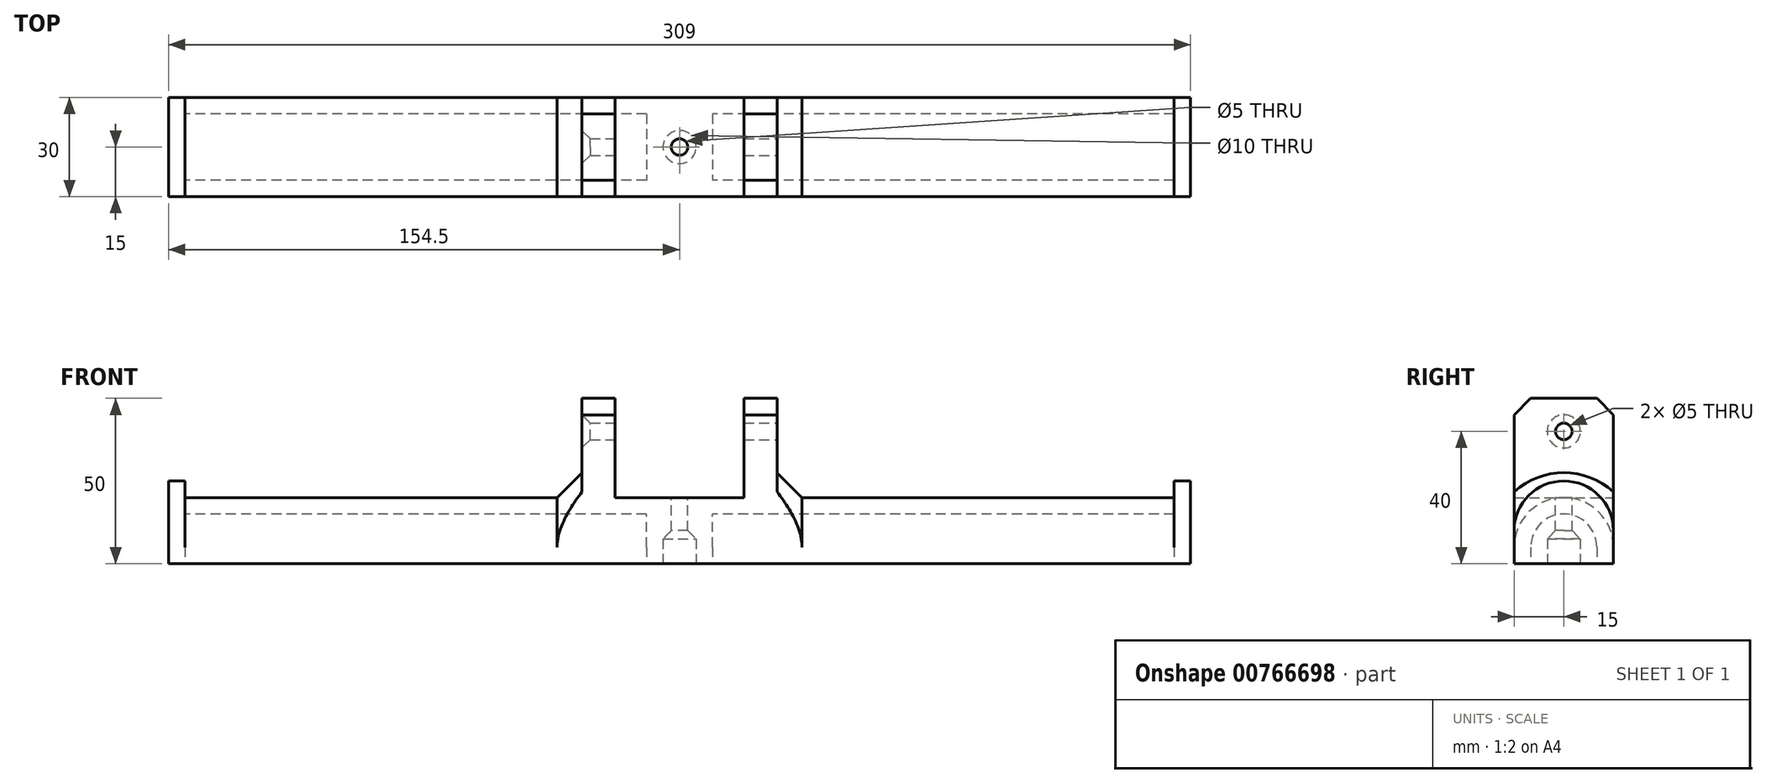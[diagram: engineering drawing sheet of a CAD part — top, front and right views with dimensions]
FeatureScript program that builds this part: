
annotation { "Feature Type Name" : "Feature", "Feature Type Description" : "" }
export const myFeature = defineFeature(function(context is Context, id is Id, definition is map)
    precondition{}
    {
        {
            var Q0;
            Q0=qCreatedBy(makeId("Front.planeOp"),FACE);
            var sketch = newSketch(context, id + "F0", { "sketchPlane" : qUnion([Q0])});
            skLineSegment(sketch, "E0", {"start": v(0, 0) * mm, "end": v(0, 100) * mm, "construction": true});
            skLineSegment(sketch, "E1", {"start": v(0, 0) * mm, "end": v(149.5, 0) * mm});
            skLineSegment(sketch, "E2", {"start": v(149.5, 0) * mm, "end": v(149.5, 20) * mm});
            skLineSegment(sketch, "E3", {"start": v(149.5, 20) * mm, "end": v(29.5, 20) * mm});
            skLineSegment(sketch, "E4", {"start": v(29.5, 20) * mm, "end": v(29.5, 50) * mm});
            skLineSegment(sketch, "E5", {"start": v(29.5, 50) * mm, "end": v(19.5, 50) * mm});
            skLineSegment(sketch, "E6", {"start": v(19.5, 50) * mm, "end": v(19.5, 20) * mm});
            skLineSegment(sketch, "E7", {"start": v(19.5, 20) * mm, "end": v(0, 20) * mm});
            skLineSegment(sketch, "E8.MirrorCS", {"start": v(0, 0) * mm, "end": v(-149.5, 0) * mm});
            skLineSegment(sketch, "E9.MirrorCS", {"start": v(-19.5, 20) * mm, "end": v(0, 20) * mm});
            skLineSegment(sketch, "E10.MirrorCS", {"start": v(-19.5, 50) * mm, "end": v(-19.5, 20) * mm});
            skLineSegment(sketch, "E11.MirrorCS", {"start": v(-149.5, 0) * mm, "end": v(-149.5, 20) * mm});
            skLineSegment(sketch, "E12.MirrorCS", {"start": v(-29.5, 20) * mm, "end": v(-29.5, 50) * mm});
            skLineSegment(sketch, "E13.MirrorCS", {"start": v(-29.5, 50) * mm, "end": v(-19.5, 50) * mm});
            skLineSegment(sketch, "E14.MirrorCS", {"start": v(-149.5, 20) * mm, "end": v(-29.5, 20) * mm});
            skSolve(sketch);
        }
        {
            var Q0;
            Q0 = qSketchRegion(id + "F0", true);
            extrude(context, id + "F1", {"entities" : qUnion([Q0]), "depth" : 30 * mm, "offsetDistance" : 25 * mm});
        }
        {
            var Q0;
            Q0=makeQuery(id+"F1.opExtrude","CAP_EDGE",EDGE,{"disambiguationData":[OSD([sQuery(id+"F0.wireOp",EDGE,"E14.MirrorCS")])],"isStart":true});
            var Q1;
            Q1=makeQuery(id+"F1.opExtrude","CAP_EDGE",EDGE,{"disambiguationData":[OSD([sQuery(id+"F0.wireOp",EDGE,"E14.MirrorCS")])],"isStart":false});
            var Q2;
            Q2=makeQuery(id+"F1.opExtrude","CAP_EDGE",EDGE,{"disambiguationData":[OSD([sQuery(id+"F0.wireOp",EDGE,"E3")])],"isStart":true});
            var Q3;
            Q3=makeQuery(id+"F1.opExtrude","CAP_EDGE",EDGE,{"disambiguationData":[OSD([sQuery(id+"F0.wireOp",EDGE,"E3")])],"isStart":false});
            fillet(context, id + "F2", {"entities" : qUnion([Q0, Q1, Q2, Q3]), "radius" : 15 * mm, "tangentPropagation" : true, "allowEdgeOverflow" : false});
        }
        {
            var Q0;
            Q0=makeQuery(id+"F1.opExtrude","SWEPT_FACE",FACE,{"disambiguationData":[OSD([sQuery(id+"F0.wireOp",EDGE,"E11.MirrorCS")])]});
            var sketch = newSketch(context, id + "F3", { "sketchPlane" : qUnion([Q0])});
            skArc(sketch, "E15.0", {"start": v(25, 5) * mm, "mid": v(15, 15) * mm, "end": v(5, 5) * mm});
            skLineSegment(sketch, "E16.bottom", {"start": v(5, 5) * mm, "end": v(25, 5) * mm, "construction": true});
            skLineSegment(sketch, "E16.top", {"start": v(5, 0) * mm, "end": v(25, 0) * mm});
            skLineSegment(sketch, "E16.left", {"start": v(5, 5) * mm, "end": v(5, 0) * mm});
            skLineSegment(sketch, "E16.right", {"start": v(25, 5) * mm, "end": v(25, 0) * mm});
            skSolve(sketch);
        }
        {
            var Q0;
            Q0 = qSketchRegion(id + "F3", true);
            extrude(context, id + "F4", {"entities" : qUnion([Q0]), "operationType" : NewBodyOperationType.REMOVE, "endBound" : BoundingType.THROUGH_ALL, "oppositeDirection" : true, "depth" : 25 * mm, "offsetDistance" : 25 * mm});
        }
        {
            var Q0;
            Q0=makeQuery(id+"F2.opFillet","BLEND_EDGE",EDGE,{"blendedFrom":[makeQuery(id+"F1.opExtrude","CAP_EDGE",EDGE,{"disambiguationData":[OSD([sQuery(id+"F0.wireOp",EDGE,"E14.MirrorCS")])],"isStart":true}),makeQuery(id+"F1.opExtrude","SWEPT_FACE",FACE,{"disambiguationData":[OSD([sQuery(id+"F0.wireOp",EDGE,"E12.MirrorCS")])]})],"blendedInto":[makeQuery(id+"F1.opExtrude","SWEPT_FACE",FACE,{"disambiguationData":[OSD([sQuery(id+"F0.wireOp",EDGE,"E12.MirrorCS")])]})]});
            var Q1;
            Q1=makeQuery(id+"F2.opFillet","BLEND_EDGE",EDGE,{"blendedFrom":[makeQuery(id+"F1.opExtrude","CAP_EDGE",EDGE,{"disambiguationData":[OSD([sQuery(id+"F0.wireOp",EDGE,"E3")])],"isStart":true}),makeQuery(id+"F1.opExtrude","SWEPT_FACE",FACE,{"disambiguationData":[OSD([sQuery(id+"F0.wireOp",EDGE,"E4")])]})],"blendedInto":[makeQuery(id+"F1.opExtrude","SWEPT_FACE",FACE,{"disambiguationData":[OSD([sQuery(id+"F0.wireOp",EDGE,"E4")])]})]});
            chamfer(context, id + "F5", {"entities" : qUnion([Q0, Q1]), "width" : 7.5 * mm, "tangentPropagation" : true});
        }
        {
            var Q0;
            Q0=makeQuery(id+"F1.opExtrude","CAP_EDGE",EDGE,{"disambiguationData":[OSD([sQuery(id+"F0.wireOp",EDGE,"E13.MirrorCS")])],"isStart":true});
            var Q1;
            Q1=makeQuery(id+"F1.opExtrude","CAP_EDGE",EDGE,{"disambiguationData":[OSD([sQuery(id+"F0.wireOp",EDGE,"E13.MirrorCS")])],"isStart":false});
            var Q2;
            Q2=makeQuery(id+"F1.opExtrude","CAP_EDGE",EDGE,{"disambiguationData":[OSD([sQuery(id+"F0.wireOp",EDGE,"E5")])],"isStart":true});
            var Q3;
            Q3=makeQuery(id+"F1.opExtrude","CAP_EDGE",EDGE,{"disambiguationData":[OSD([sQuery(id+"F0.wireOp",EDGE,"E5")])],"isStart":false});
            chamfer(context, id + "F6", {"entities" : qUnion([Q0, Q1, Q2, Q3]), "width" : 5 * mm, "tangentPropagation" : true});
        }
        {
            var Q0;
            Q0=makeQuery(id+"F1.opExtrude","SWEPT_FACE",FACE,{"disambiguationData":[OSD([sQuery(id+"F0.wireOp",EDGE,"E4")])]});
            var sketch = newSketch(context, id + "F7", { "sketchPlane" : qUnion([Q0])});
            skCircle(sketch, "E17", {"center": v(-15, 40) * mm, "radius": 2.5 * mm});
            skPoint(sketch, "E17.centerSnap0", {"position": v(-15, 50) * mm});
            skSolve(sketch);
        }
        {
            var Q0;
            Q0 = qSketchRegion(id + "F7", true);
            extrude(context, id + "F8", {"entities" : qUnion([Q0]), "operationType" : NewBodyOperationType.REMOVE, "endBound" : BoundingType.THROUGH_ALL, "oppositeDirection" : true, "depth" : 25 * mm, "offsetDistance" : 25 * mm});
        }
        {
            var Q0;
            {var subQ1=sQuery(id+"F0.wireOp",EDGE,"E8.MirrorCS");var subQ3=sQuery(id+"F0.wireOp",EDGE,"E1");Q0=makeQuery(id+"F4.boolean.opBoolean","SPLIT",FACE,{"disambiguationData":[TD([makeQuery(id+"F4.opExtrude","SWEPT_FACE",FACE,{"disambiguationData":[OSD([sQuery(id+"F3.wireOp",EDGE,"E16.right")])]})])],"derivedFrom":makeQuery(id+"F1.opExtrude","SWEPT_FACE",FACE,{"disambiguationData":[OSD([subQ3,subQ1])]})});}
            var sketch = newSketch(context, id + "F9", { "sketchPlane" : qUnion([Q0])});
            skLineSegment(sketch, "E18.0.0", {"start": v(19.5, 0) * mm, "end": v(-19.5, 0) * mm, "construction": true});
            skLineSegment(sketch, "E18.0.1", {"start": v(-19.5, 0) * mm, "end": v(-19.5, 30) * mm, "construction": true});
            skLineSegment(sketch, "E18.0.2", {"start": v(-19.5, 30) * mm, "end": v(19.5, 30) * mm, "construction": true});
            skLineSegment(sketch, "E18.0.3", {"start": v(19.5, 30) * mm, "end": v(19.5, 0) * mm, "construction": true});
            skLineSegment(sketch, "E19.bottom", {"start": v(10, 5) * mm, "end": v(-10, 5) * mm});
            skLineSegment(sketch, "E19.top", {"start": v(10, 25) * mm, "end": v(-10, 25) * mm});
            skLineSegment(sketch, "E19.left", {"start": v(10, 5) * mm, "end": v(10, 25) * mm});
            skLineSegment(sketch, "E19.right", {"start": v(-10, 5) * mm, "end": v(-10, 25) * mm});
            skPoint(sketch, "E19.middle", {"position": v(0, 15) * mm});
            skSolve(sketch);
        }
        {
            var Q0;
            Q0 = qSketchRegion(id + "F9", true);
            var Q1;
            Q1=makeQuery(id+"F4.boolean.opBoolean","COPY",FACE,{"derivedFrom":makeQuery(id+"F4.opExtrude","SWEPT_FACE",FACE,{"disambiguationData":[OSD([sQuery(id+"F3.wireOp",EDGE,"E15.0")])]})});
            extrude(context, id + "F10", {"entities" : qUnion([Q0]), "operationType" : NewBodyOperationType.ADD, "endBound" : BoundingType.UP_TO_SURFACE, "oppositeDirection" : true, "depth" : 25 * mm, "endBoundEntityFace" : qUnion([Q1]), "offsetDistance" : 25 * mm});
        }
        {
            var Q0;
            Q0=makeQuery(id+"F1.opExtrude","SWEPT_FACE",FACE,{"disambiguationData":[OSD([sQuery(id+"F0.wireOp",EDGE,"E7"),sQuery(id+"F0.wireOp",EDGE,"E9.MirrorCS")])]});
            var sketch = newSketch(context, id + "F11", { "sketchPlane" : qUnion([Q0])});
            skCircle(sketch, "E20", {"center": v(0, -15) * mm, "radius": 2.5 * mm});
            skPoint(sketch, "E20.centerSnap0", {"position": v(19.5, -15) * mm});
            skSolve(sketch);
        }
        {
            var Q0;
            Q0 = qSketchRegion(id + "F11", true);
            extrude(context, id + "F12", {"entities" : qUnion([Q0]), "operationType" : NewBodyOperationType.REMOVE, "endBound" : BoundingType.THROUGH_ALL, "oppositeDirection" : true, "depth" : 25 * mm, "offsetDistance" : 25 * mm});
        }
        {
            var Q0;
            Q0=makeQuery(id+"F8.boolean.opBoolean","INTERSECT",EDGE,{"derivedFrom":[makeQuery(id+"F1.opExtrude","SWEPT_FACE",FACE,{"disambiguationData":[OSD([sQuery(id+"F0.wireOp",EDGE,"E12.MirrorCS")])]}),makeQuery(id+"F8.opExtrude","SWEPT_FACE",FACE,{"disambiguationData":[OSD([sQuery(id+"F7.wireOp",EDGE,"E17")])]})]});
            var Q1;
            Q1=makeQuery(id+"F8.boolean.opBoolean","COPY",EDGE,{"derivedFrom":makeQuery(id+"F8.opExtrude","CAP_EDGE",EDGE,{"disambiguationData":[OSD([sQuery(id+"F7.wireOp",EDGE,"E17")])],"isStart":true})});
            chamfer(context, id + "F13", {"entities" : qUnion([Q0, Q1]), "width" : 2.5 * mm, "tangentPropagation" : true});
        }
        {
            var Q0;
            Q0=makeQuery(id+"F1.opExtrude","CAP_FACE",FACE,{"disambiguationData":[OSD([sQuery(id+"F0.wireOp",EDGE,"E1"),sQuery(id+"F0.wireOp",EDGE,"E2"),sQuery(id+"F0.wireOp",EDGE,"E3"),sQuery(id+"F0.wireOp",EDGE,"E4"),sQuery(id+"F0.wireOp",EDGE,"E5"),sQuery(id+"F0.wireOp",EDGE,"E6"),sQuery(id+"F0.wireOp",EDGE,"E7"),sQuery(id+"F0.wireOp",EDGE,"E8.MirrorCS"),sQuery(id+"F0.wireOp",EDGE,"E9.MirrorCS"),sQuery(id+"F0.wireOp",EDGE,"E10.MirrorCS"),sQuery(id+"F0.wireOp",EDGE,"E11.MirrorCS"),sQuery(id+"F0.wireOp",EDGE,"E12.MirrorCS"),sQuery(id+"F0.wireOp",EDGE,"E13.MirrorCS"),sQuery(id+"F0.wireOp",EDGE,"E14.MirrorCS")])],"isStart":false});
            var sketch = newSketch(context, id + "F14", { "sketchPlane" : qUnion([Q0])});
            skLineSegment(sketch, "E21.bottom", {"start": v(-149.5, 0) * mm, "end": v(-154.5, 0) * mm});
            skLineSegment(sketch, "E21.top", {"start": v(-149.5, 25) * mm, "end": v(-154.5, 25) * mm});
            skLineSegment(sketch, "E21.left", {"start": v(-149.5, 0) * mm, "end": v(-149.5, 25) * mm});
            skLineSegment(sketch, "E21.right", {"start": v(-154.5, 0) * mm, "end": v(-154.5, 25) * mm});
            skLineSegment(sketch, "E22.bottom", {"start": v(149.5, 0) * mm, "end": v(154.5, 0) * mm});
            skLineSegment(sketch, "E22.top", {"start": v(149.5, 25) * mm, "end": v(154.5, 25) * mm});
            skLineSegment(sketch, "E22.left", {"start": v(149.5, 0) * mm, "end": v(149.5, 25) * mm});
            skLineSegment(sketch, "E22.right", {"start": v(154.5, 0) * mm, "end": v(154.5, 25) * mm});
            skSolve(sketch);
        }
        {
            var Q0;
            Q0 = qSketchRegion(id + "F14", true);
            var Q1;
            Q1=makeQuery(id+"F1.opExtrude","CAP_FACE",FACE,{"disambiguationData":[OSD([sQuery(id+"F0.wireOp",EDGE,"E1"),sQuery(id+"F0.wireOp",EDGE,"E2"),sQuery(id+"F0.wireOp",EDGE,"E3"),sQuery(id+"F0.wireOp",EDGE,"E4"),sQuery(id+"F0.wireOp",EDGE,"E5"),sQuery(id+"F0.wireOp",EDGE,"E6"),sQuery(id+"F0.wireOp",EDGE,"E7"),sQuery(id+"F0.wireOp",EDGE,"E8.MirrorCS"),sQuery(id+"F0.wireOp",EDGE,"E9.MirrorCS"),sQuery(id+"F0.wireOp",EDGE,"E10.MirrorCS"),sQuery(id+"F0.wireOp",EDGE,"E11.MirrorCS"),sQuery(id+"F0.wireOp",EDGE,"E12.MirrorCS"),sQuery(id+"F0.wireOp",EDGE,"E13.MirrorCS"),sQuery(id+"F0.wireOp",EDGE,"E14.MirrorCS")])],"isStart":true});
            extrude(context, id + "F15", {"entities" : qUnion([Q0]), "operationType" : NewBodyOperationType.ADD, "endBound" : BoundingType.UP_TO_SURFACE, "oppositeDirection" : true, "depth" : 25 * mm, "endBoundEntityFace" : qUnion([Q1]), "offsetDistance" : 25 * mm});
        }
        {
            var Q0;
            Q0=makeQuery(id+"F15.opExtrude","CAP_EDGE",EDGE,{"disambiguationData":[OSD([sQuery(id+"F14.wireOp",EDGE,"E22.top")])],"isStart":false});
            var Q1;
            Q1=makeQuery(id+"F15.opExtrude","CAP_EDGE",EDGE,{"disambiguationData":[OSD([sQuery(id+"F14.wireOp",EDGE,"E22.top")])],"isStart":true});
            var Q2;
            Q2=makeQuery(id+"F15.opExtrude","CAP_EDGE",EDGE,{"disambiguationData":[OSD([sQuery(id+"F14.wireOp",EDGE,"E21.top")])],"isStart":true});
            var Q3;
            Q3=makeQuery(id+"F15.opExtrude","CAP_EDGE",EDGE,{"disambiguationData":[OSD([sQuery(id+"F14.wireOp",EDGE,"E21.top")])],"isStart":false});
            fillet(context, id + "F16", {"entities" : qUnion([Q0, Q1, Q2, Q3]), "radius" : 15 * mm, "tangentPropagation" : true, "allowEdgeOverflow" : false});
        }
        {
            var Q0;
            {var subQ6=sQuery(id+"F0.wireOp",EDGE,"E8.MirrorCS");var subQ13=sQuery(id+"F0.wireOp",EDGE,"E1");var subQ16=makeQuery(id+"F1.opExtrude","SWEPT_FACE",FACE,{"disambiguationData":[OSD([subQ13,subQ6])]});Q0=makeQuery(id+"F15.boolean.opBoolean","MERGE",FACE,{"derivedFrom":[makeQuery(id+"F10.boolean.opBoolean","MERGE",FACE,{"derivedFrom":[makeQuery(id+"F4.boolean.opBoolean","SPLIT",FACE,{"disambiguationData":[TD([makeQuery(id+"F4.opExtrude","SWEPT_FACE",FACE,{"disambiguationData":[OSD([sQuery(id+"F3.wireOp",EDGE,"E16.left")])]})])],"derivedFrom":subQ16}),makeQuery(id+"F4.boolean.opBoolean","SPLIT",FACE,{"disambiguationData":[TD([makeQuery(id+"F4.opExtrude","SWEPT_FACE",FACE,{"disambiguationData":[OSD([sQuery(id+"F3.wireOp",EDGE,"E16.right")])]})])],"derivedFrom":subQ16}),makeQuery(id+"F10.opExtrude","CAP_FACE",FACE,{"disambiguationData":[OSD([sQuery(id+"F9.wireOp",EDGE,"E19.bottom"),sQuery(id+"F9.wireOp",EDGE,"E19.top"),sQuery(id+"F9.wireOp",EDGE,"E19.left"),sQuery(id+"F9.wireOp",EDGE,"E19.right")])],"isStart":true})]}),makeQuery(id+"F15.opExtrude","SWEPT_FACE",FACE,{"disambiguationData":[OSD([sQuery(id+"F14.wireOp",EDGE,"E21.bottom")])]}),makeQuery(id+"F15.opExtrude","SWEPT_FACE",FACE,{"disambiguationData":[OSD([sQuery(id+"F14.wireOp",EDGE,"E22.bottom")])]})]});}
            var sketch = newSketch(context, id + "F17", { "sketchPlane" : qUnion([Q0])});
            skCircle(sketch, "E23", {"center": v(0, 15) * mm, "radius": 5 * mm});
            skSolve(sketch);
        }
        {
            var Q0;
            Q0 = qSketchRegion(id + "F17", true);
            extrude(context, id + "F18", {"entities" : qUnion([Q0]), "operationType" : NewBodyOperationType.REMOVE, "oppositeDirection" : true, "depth" : 7.5 * mm, "offsetDistance" : 25 * mm});
        }
        {
            var Q0;
            Q0=makeQuery(id+"F18.boolean.opBoolean","INTERSECT",EDGE,{"derivedFrom":[makeQuery(id+"F12.boolean.opBoolean","COPY",FACE,{"derivedFrom":makeQuery(id+"F12.opExtrude","SWEPT_FACE",FACE,{"disambiguationData":[OSD([sQuery(id+"F11.wireOp",EDGE,"E20")])]})}),makeQuery(id+"F18.opExtrude","CAP_FACE",FACE,{"disambiguationData":[OSD([sQuery(id+"F17.wireOp",EDGE,"E23")])],"isStart":false})]});
            chamfer(context, id + "F19", {"entities" : qUnion([Q0]), "width" : 2.5 * mm, "tangentPropagation" : true});
        }
    });
